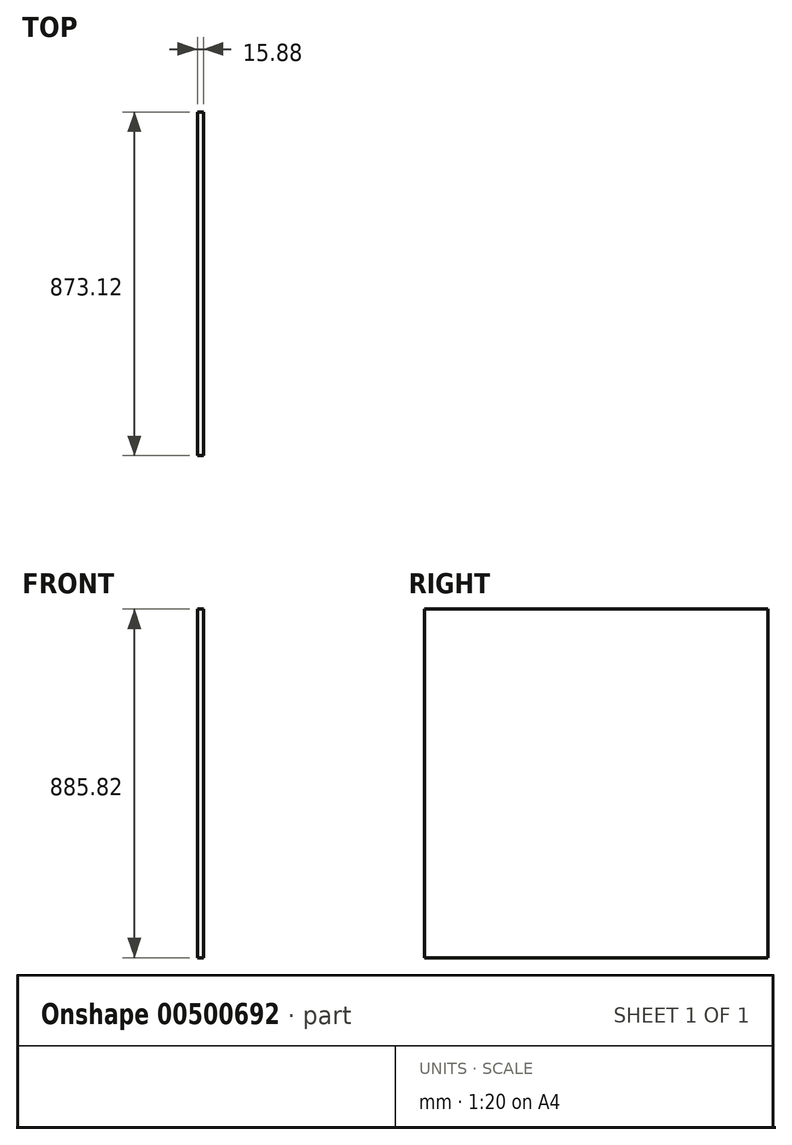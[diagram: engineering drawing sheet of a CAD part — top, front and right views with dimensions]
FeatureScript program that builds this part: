
annotation { "Feature Type Name" : "Feature", "Feature Type Description" : "" }
export const myFeature = defineFeature(function(context is Context, id is Id, definition is map)
    precondition{}
    {
        {
            var Q0;
            Q0=qCreatedBy(makeId("Right.planeOp"),FACE);
            var sketch = newSketch(context, id + "F0", { "sketchPlane" : qUnion([Q0])});
            skLineSegment(sketch, "E0.bottom", {"start": v(0, 0) * mm, "end": v(873.12, 0) * mm});
            skLineSegment(sketch, "E0.top", {"start": v(0, 885.83) * mm, "end": v(873.12, 885.83) * mm});
            skLineSegment(sketch, "E0.left", {"start": v(0, 0) * mm, "end": v(0, 885.83) * mm});
            skLineSegment(sketch, "E0.right", {"start": v(873.12, 0) * mm, "end": v(873.12, 885.83) * mm});
            skSolve(sketch);
        }
        {
            var Q0;
            Q0=makeQuery(id+"F0.imprint","IMPRINT",FACE,{"disambiguationData":[TD([[makeQuery(id+"F0.imprint","IMPRINT",EDGE,{"derivedFrom":sQuery(id+"F0.wireOp",EDGE,"E0.bottom")}),1.0]])]});
            extrude(context, id + "F1", {"entities" : qUnion([Q0]), "oppositeDirection" : true, "depth" : 15.88 * mm, "offsetDistance" : 25.4 * mm});
        }
    });
